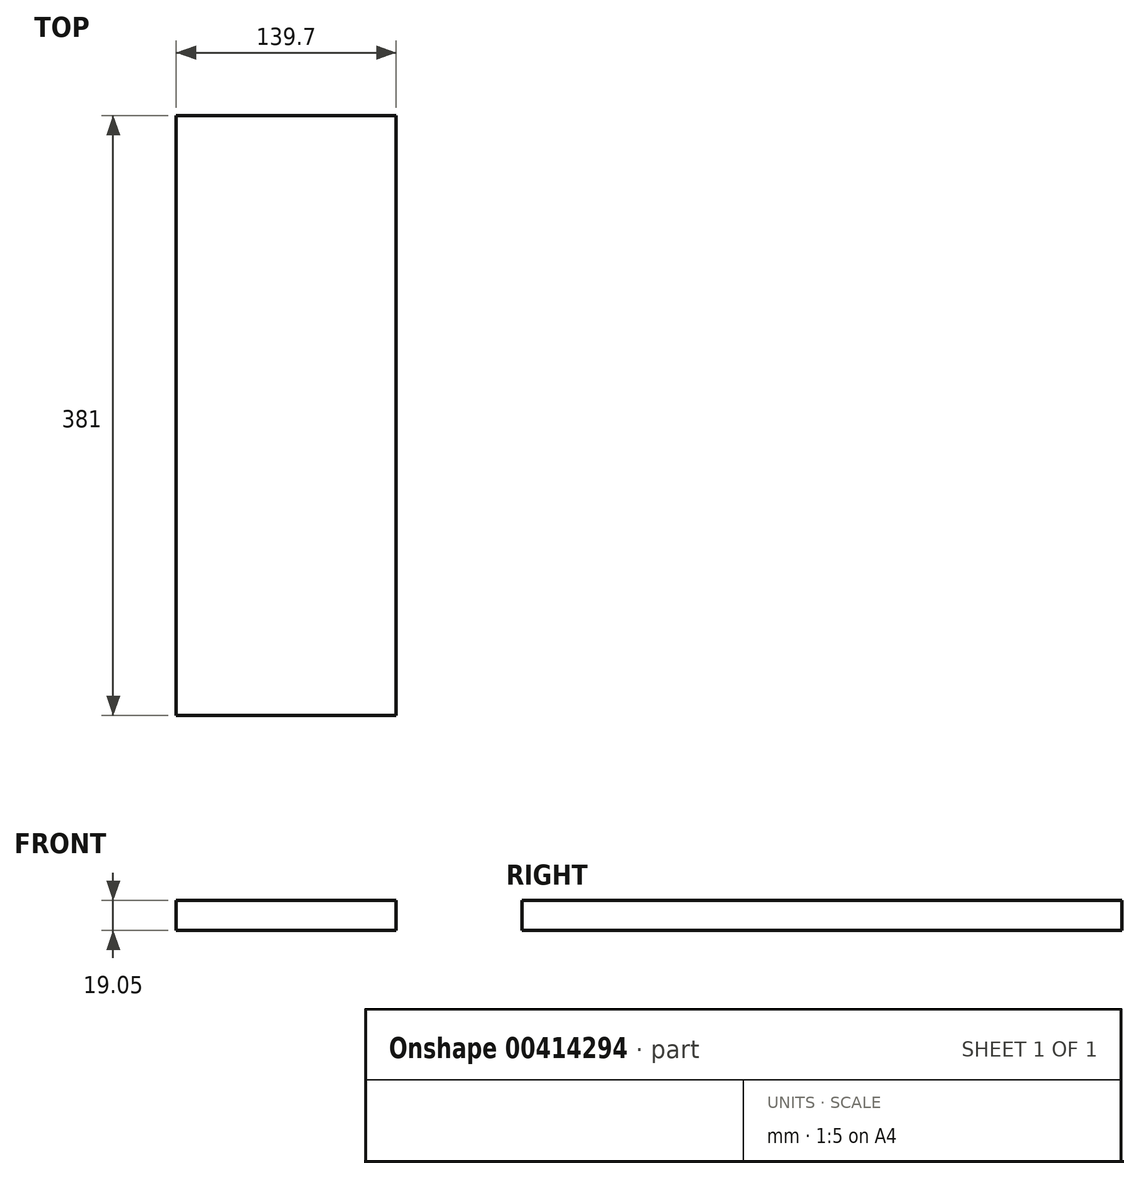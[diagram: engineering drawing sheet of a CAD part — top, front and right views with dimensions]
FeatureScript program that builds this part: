
annotation { "Feature Type Name" : "Feature", "Feature Type Description" : "" }
export const myFeature = defineFeature(function(context is Context, id is Id, definition is map)
    precondition{}
    {
        {
            var Q0;
            Q0=qCreatedBy(makeId("Front.planeOp"),FACE);
            var sketch = newSketch(context, id + "F0", { "sketchPlane" : qUnion([Q0])});
            skLineSegment(sketch, "E0.bottom", {"start": v(0, 0) * mm, "end": v(-139.7, 0) * mm});
            skLineSegment(sketch, "E0.top", {"start": v(0, 19.05) * mm, "end": v(-139.7, 19.05) * mm});
            skLineSegment(sketch, "E0.left", {"start": v(0, 0) * mm, "end": v(0, 19.05) * mm});
            skLineSegment(sketch, "E0.right", {"start": v(-139.7, 0) * mm, "end": v(-139.7, 19.05) * mm});
            skSolve(sketch);
        }
        {
            var Q0;
            Q0=qSketchRegion(id+"F0",true);
            extrude(context, id + "F1", {"entities" : qUnion([Q0]), "depth" : 381 * mm});
        }
    });
